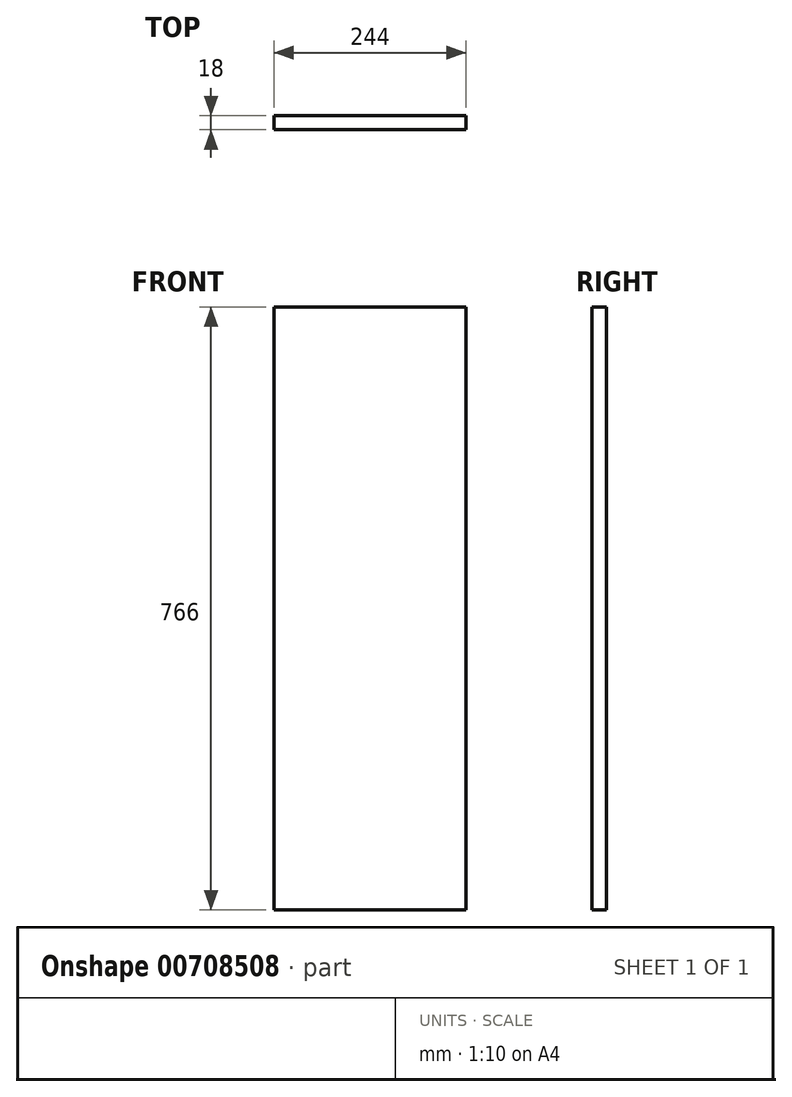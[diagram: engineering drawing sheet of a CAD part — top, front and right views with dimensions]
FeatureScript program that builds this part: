
annotation { "Feature Type Name" : "Feature", "Feature Type Description" : "" }
export const myFeature = defineFeature(function(context is Context, id is Id, definition is map)
    precondition{}
    {
        {
            var Q0;
            Q0=qCreatedBy(makeId("Front.planeOp"),FACE);
            var sketch = newSketch(context, id + "F0", { "sketchPlane" : qUnion([Q0])});
            skLineSegment(sketch, "E0.bottom", {"start": v(0, 0) * mm, "end": v(-244, 0) * mm});
            skLineSegment(sketch, "E0.top", {"start": v(0, -766) * mm, "end": v(-244, -766) * mm});
            skLineSegment(sketch, "E0.left", {"start": v(0, 0) * mm, "end": v(0, -766) * mm});
            skLineSegment(sketch, "E0.right", {"start": v(-244, 0) * mm, "end": v(-244, -766) * mm});
            skSolve(sketch);
        }
        {
            var Q0;
            Q0=qSketchRegion(id+"F0",true);
            extrude(context, id + "F1", {"entities" : qUnion([Q0]), "depth" : 18 * mm, "offsetDistance" : 25 * mm});
        }
    });
